annotation { "Feature Type Name" : "Feature", "Feature Type Description" : "" }
export const myFeature = defineFeature(function(context is Context, id is Id, definition is map)
    precondition{}
    {
        {
            var Q0;
            Q0=qCreatedBy(makeId("Top.planeOp"),FACE);
            var sketch = newSketch(context, id + "F0", { "sketchPlane" : qUnion([Q0])});
            skLineSegment(sketch, "E0", {"start": v(0, 56.35) * mm, "end": v(0, -56.35) * mm});
            skLineSegment(sketch, "E1", {"start": v(56.35, 0) * mm, "end": v(-56.35, 0) * mm});
            skPoint(sketch, "E2", {"position": v(0, 0) * mm});
            skPoint(sketch, "E3", {"position": v(-22.39, -33.62) * mm});
            skPoint(sketch, "E4", {"position": v(-22.39, 33.48) * mm});
            skPoint(sketch, "E5", {"position": v(21.85, 33.48) * mm});
            skLineSegment(sketch, "E6", {"start": v(1.95, 33.48) * mm, "end": v(7.67, 33.48) * mm});
            skLineSegment(sketch, "E7", {"start": v(21.85, -33.62) * mm, "end": v(1.95, -33.62) * mm});
            skLineSegment(sketch, "E8", {"start": v(21.85, 18.05) * mm, "end": v(21.85, 17.68) * mm});
            skLineSegment(sketch, "E9", {"start": v(-2.74, 33.48) * mm, "end": v(-21.16, 33.48) * mm});
            skLineSegment(sketch, "E10", {"start": v(-22.39, -33.62) * mm, "end": v(-10.07, -33.62) * mm});
            skLineSegment(sketch, "E11", {"start": v(-22.39, -2.3) * mm, "end": v(-22.39, -33.62) * mm});
            skPoint(sketch, "E12", {"position": v(-22.39, 31.95) * mm});
            skPoint(sketch, "E12.positionSnap0", {"position": v(-21.16, 31.95) * mm});
            skArc(sketch, "E13", {"start": v(-21.16, 33.48) * mm, "mid": v(-22.39, 31.95) * mm, "end": v(-21.16, 30.43) * mm});
            skPoint(sketch, "E14", {"position": v(-2.74, 33.48) * mm});
            skPoint(sketch, "E15", {"position": v(-7.3, 30.43) * mm});
            skLineSegment(sketch, "E16", {"start": v(-21.16, 30.43) * mm, "end": v(-7.3, 30.43) * mm});
            skPoint(sketch, "E17", {"position": v(-11.04, 20.68) * mm});
            skPoint(sketch, "E18", {"position": v(-9.45, 18.3) * mm});
            skPoint(sketch, "E19", {"position": v(-9.45, 25.39) * mm});
            skFitSpline(sketch, "E20", {"points": [v(-9.45, 25.39) * mm, v(-11.04, 20.68) * mm, v(-9.45, 18.3) * mm], "startDerivative": vector(-4.65, -9.06) * mm, "endDerivative": vector(5.1, -4.94) * mm});
            skLineSegment(sketch, "E21", {"start": v(-7.3, 30.43) * mm, "end": v(-9.45, 25.39) * mm});
            skPoint(sketch, "E22", {"position": v(-19.2, 12.85) * mm});
            skPoint(sketch, "E23", {"position": v(-12.14, 4.7) * mm});
            skArc(sketch, "E24", {"start": v(-19.2, 12.85) * mm, "mid": v(-8.74, 5.6) * mm, "end": v(-9.45, 18.3) * mm});
            skPoint(sketch, "E25", {"position": v(-8.14, 21.15) * mm});
            skPoint(sketch, "E26", {"position": v(-7.55, 20.43) * mm});
            skPoint(sketch, "E27", {"position": v(-7.55, 22.7) * mm});
            skFitSpline(sketch, "E28", {"points": [v(-7.55, 22.7) * mm, v(-8.14, 21.15) * mm, v(-7.55, 20.43) * mm], "startDerivative": vector(-1.74, -3) * mm, "endDerivative": vector(1.9, -1.47) * mm});
            skLineSegment(sketch, "E29", {"start": v(-2.74, 33.48) * mm, "end": v(-7.55, 22.7) * mm});
            skArc(sketch, "E30.0", {"start": v(-21.98, 12.85) * mm, "mid": v(-7.57, 3.08) * mm, "end": v(-7.62, 20.5) * mm});
            skPoint(sketch, "E31", {"position": v(-21.98, 12.85) * mm});
            skPoint(sketch, "E32", {"position": v(-20.63, 13.93) * mm});
            skArc(sketch, "E33", {"start": v(-19.2, 12.85) * mm, "mid": v(-20.59, 13.94) * mm, "end": v(-21.98, 12.85) * mm});
            skLineSegment(sketch, "E34", {"start": v(1.95, 33.48) * mm, "end": v(1.95, 2.25) * mm});
            skPoint(sketch, "E35", {"position": v(21.85, 18.05) * mm});
            skArc(sketch, "E36", {"start": v(13.56, 3.8) * mm, "mid": v(21.85, 17.87) * mm, "end": v(13.56, 31.93) * mm});
            skPoint(sketch, "E37", {"position": v(7.67, 33.48) * mm});
            skPoint(sketch, "E38", {"position": v(13.56, 31.93) * mm});
            skPoint(sketch, "E39", {"position": v(13.56, 3.8) * mm});
            skArc(sketch, "E40.0", {"start": v(5.03, 4.88) * mm, "mid": v(9.62, 5.44) * mm, "end": v(13.73, 7.58) * mm});
            skLineSegment(sketch, "E40.1", {"start": v(5.03, 27.26) * mm, "end": v(5.03, 4.88) * mm});
            skLineSegment(sketch, "E41", {"start": v(5.03, 27.26) * mm, "end": v(13.73, 7.58) * mm});
            skLineSegment(sketch, "E42", {"start": v(16.04, 9.89) * mm, "end": v(6.78, 30.83) * mm});
            skLineSegment(sketch, "E43", {"start": v(-22.39, -2.3) * mm, "end": v(-10.07, -2.3) * mm});
            skLineSegment(sketch, "E44", {"start": v(1.95, -2.3) * mm, "end": v(1.95, -33.62) * mm});
            skLineSegment(sketch, "E45", {"start": v(1.95, -2.3) * mm, "end": v(22.67, -2.3) * mm});
            skLineSegment(sketch, "E46", {"start": v(22.67, -2.3) * mm, "end": v(15.49, -17.1) * mm});
            skFitSpline(sketch, "E47", {"points": [v(15.49, -17.1) * mm, v(15.2, -17.6) * mm, v(15.17, -17.96) * mm], "startDerivative": vector(-0.63, -0.9) * mm, "endDerivative": vector(0.03, -0.82) * mm});
            skLineSegment(sketch, "E48.MirrorCS", {"start": v(1.95, -33.62) * mm, "end": v(22.67, -33.62) * mm});
            skLineSegment(sketch, "E49.MirrorCS", {"start": v(22.67, -33.62) * mm, "end": v(15.49, -18.82) * mm});
            skFitSpline(sketch, "E50.MirrorCS", {"points": [v(15.49, -18.82) * mm, v(15.2, -18.34) * mm, v(15.17, -17.96) * mm], "startDerivative": vector(-0.63, 0.9) * mm, "endDerivative": vector(0.03, 0.82) * mm});
            skArc(sketch, "E51", {"start": v(-5.17, -17.31) * mm, "mid": v(-2.75, -8.22) * mm, "end": v(-10.07, -2.3) * mm});
            skFitSpline(sketch, "E52", {"points": [v(-5.17, -17.31) * mm, v(-5.38, -17.68) * mm, v(-5.4, -17.96) * mm], "startDerivative": vector(-0.48, -0.68) * mm, "endDerivative": vector(0.02, -0.62) * mm});
            skArc(sketch, "E53.MirrorCS", {"start": v(-5.17, -18.61) * mm, "mid": v(-2.75, -27.7) * mm, "end": v(-10.07, -33.62) * mm});
            skFitSpline(sketch, "E54.MirrorCS", {"points": [v(-5.17, -18.61) * mm, v(-5.38, -18.25) * mm, v(-5.4, -17.96) * mm], "startDerivative": vector(-0.48, 0.68) * mm, "endDerivative": vector(0.02, 0.62) * mm});
            skPoint(sketch, "E55.end.orphan", {"position": v(-10.07, -33.62) * mm});
            skPoint(sketch, "E56.orphan", {"position": v(-10.07, -17.96) * mm});
            skPoint(sketch, "E57.orphan", {"position": v(0, -33.62) * mm});
            skLineSegment(sketch, "E58.MirrorCS", {"start": v(0, 2.62) * mm, "end": v(7.67, 2.62) * mm});
            skArc(sketch, "E59.trimOffspring", {"start": v(16.04, 9.89) * mm, "mid": v(17.67, 23.12) * mm, "end": v(6.78, 30.83) * mm});
            skPoint(sketch, "E60", {"position": v(7.67, 2.62) * mm});
            skFitSpline(sketch, "E61", {"points": [v(13.56, 3.8) * mm, v(10.55, 2.81) * mm, v(7.67, 2.62) * mm], "startDerivative": vector(-5.9, -2.33) * mm, "endDerivative": vector(-5.9, -0.02) * mm});
            skPoint(sketch, "E62.1.internal.snap0", {"position": v(9.38, 17.42) * mm});
            skFitSpline(sketch, "E62", {"points": [v(13.56, 31.93) * mm, v(9.38, 33.27) * mm, v(7.67, 33.48) * mm], "startDerivative": vector(-7.54, 2.7) * mm, "endDerivative": vector(-3.99, 0.22) * mm});
            skPoint(sketch, "E63.orphan", {"position": v(10.87, 2.62) * mm});
            skPoint(sketch, "E64.orphan", {"position": v(0, 33.48) * mm});
            skPoint(sketch, "E65.trimOffspring.start.orphan", {"position": v(21.85, 2.62) * mm});
            skLineSegment(sketch, "E66", {"start": v(-27.8, 0) * mm, "end": v(-27.8, 46.45) * mm});
            skLineSegment(sketch, "E67", {"start": v(-27.8, 46.45) * mm, "end": v(0, 46.45) * mm});
            skLineSegment(sketch, "E68.MirrorCS", {"start": v(27.8, 0) * mm, "end": v(27.8, 46.45) * mm});
            skLineSegment(sketch, "E69.MirrorCS", {"start": v(-27.8, -46.45) * mm, "end": v(0, -46.45) * mm});
            skLineSegment(sketch, "E70.MirrorCS", {"start": v(-27.8, 0) * mm, "end": v(-27.8, -46.45) * mm});
            skLineSegment(sketch, "E71.MirrorCS", {"start": v(27.8, 46.45) * mm, "end": v(0, 46.45) * mm});
            skLineSegment(sketch, "E72.MirrorCS", {"start": v(27.8, 0) * mm, "end": v(27.8, -46.45) * mm});
            skLineSegment(sketch, "E73.MirrorCS", {"start": v(27.8, -46.45) * mm, "end": v(0, -46.45) * mm});
            skSolve(sketch);
        }
        {
            var Q0;
            Q0=qCreatedBy(makeId("Top.planeOp"),FACE);
            var sketch = newSketch(context, id + "F1", { "sketchPlane" : qUnion([Q0])});
            skLineSegment(sketch, "E74.bottom", {"start": v(-27.8, 46.45) * mm, "end": v(27.8, 46.45) * mm});
            skLineSegment(sketch, "E74.top", {"start": v(-27.8, -46.45) * mm, "end": v(27.8, -46.45) * mm});
            skLineSegment(sketch, "E74.left", {"start": v(-27.8, 46.45) * mm, "end": v(-27.8, -46.45) * mm});
            skLineSegment(sketch, "E74.right", {"start": v(27.8, 46.45) * mm, "end": v(27.8, -46.45) * mm});
            skSolve(sketch);
        }
        {
            var Q0;
            Q0=makeQuery(id+"F1.imprint","IMPRINT",FACE,{"disambiguationData":[TD([[makeQuery(id+"F1.imprint","IMPRINT",EDGE,{"derivedFrom":sQuery(id+"F1.wireOp",EDGE,"E74.bottom")}),-1.0]])]});
            extrude(context, id + "F2", {"entities" : qUnion([Q0]), "oppositeDirection" : true, "depth" : 19.05 * mm, "offsetDistance" : 25.4 * mm});
        }
        {
            var Q0;
            {var subQ7=sQuery(id+"F0.wireOp",EDGE,"E6");Q0=makeQuery(id+"F0.imprint","IMPRINT",FACE,{"disambiguationData":[TD([[makeQuery(id+"F0.imprint","IMPRINT",EDGE,{"derivedFrom":subQ7}),-1.0]])]});}
            var Q1;
            Q1=makeQuery(id+"F0.imprint","IMPRINT",FACE,{"disambiguationData":[TD([[makeQuery(id+"F0.imprint","IMPRINT",EDGE,{"derivedFrom":sQuery(id+"F0.wireOp",EDGE,"E9")}),1.0]])]});
            var Q2;
            {var subQ0=sQuery(id+"F0.wireOp",EDGE,"E44");Q2=makeQuery(id+"F0.imprint","IMPRINT",FACE,{"disambiguationData":[TD([[makeQuery(id+"F0.imprint","IMPRINT",EDGE,{"derivedFrom":subQ0}),1.0]])]});}
            var Q3;
            Q3=makeQuery(id+"F0.imprint","IMPRINT",FACE,{"disambiguationData":[TD([[makeQuery(id+"F0.imprint","IMPRINT",EDGE,{"derivedFrom":sQuery(id+"F0.wireOp",EDGE,"E10")}),1.0]])]});
            extrude(context, id + "F3", {"entities" : qUnion([Q0, Q1, Q2, Q3]), "operationType" : NewBodyOperationType.ADD, "depth" : 5.08 * mm, "offsetDistance" : 25.4 * mm});
        }
        {
            var Q0;
            {var subQ3=sQuery(id+"F1.wireOp",EDGE,"E74.bottom");var subQ5=sQuery(id+"F1.wireOp",EDGE,"E74.left");var subQ6=sQuery(id+"F1.wireOp",EDGE,"E74.top");var subQ7=sQuery(id+"F1.wireOp",EDGE,"E74.right");Q0=makeQuery(id+"F3.boolean.opBoolean","SPLIT",FACE,{"disambiguationData":[TD([makeQuery(id+"F2.opExtrude","SWEPT_FACE",FACE,{"disambiguationData":[OSD([subQ3])]})])],"derivedFrom":makeQuery(id+"F2.opExtrude","CAP_FACE",FACE,{"disambiguationData":[OSD([subQ3,subQ6,subQ5,subQ7])],"isStart":true})});}
            var sketch = newSketch(context, id + "F4", { "sketchPlane" : qUnion([Q0])});
            skLineSegment(sketch, "E75", {"start": v(-27.8, 36.27) * mm, "end": v(27.8, 36.27) * mm});
            skLineSegment(sketch, "E76", {"start": v(-27.8, 36.27) * mm, "end": v(-27.8, 50.24) * mm});
            skLineSegment(sketch, "E77", {"start": v(-27.8, 50.24) * mm, "end": v(27.8, 50.24) * mm});
            skLineSegment(sketch, "E78", {"start": v(27.8, 50.24) * mm, "end": v(27.8, 36.27) * mm});
            skLineSegment(sketch, "E79.0", {"start": v(-24.8, 47.24) * mm, "end": v(24.8, 47.24) * mm});
            skLineSegment(sketch, "E79.1", {"start": v(-24.8, 39.27) * mm, "end": v(-24.8, 47.24) * mm});
            skLineSegment(sketch, "E79.2", {"start": v(-24.8, 39.27) * mm, "end": v(24.8, 39.27) * mm});
            skLineSegment(sketch, "E79.3", {"start": v(24.8, 47.24) * mm, "end": v(24.8, 39.27) * mm});
            skLineSegment(sketch, "E80", {"start": v(0, 0) * mm, "end": v(41.07, 0) * mm});
            skLineSegment(sketch, "E81.MirrorCS", {"start": v(-27.8, -50.24) * mm, "end": v(27.8, -50.24) * mm});
            skLineSegment(sketch, "E82.MirrorCS", {"start": v(-27.8, -36.27) * mm, "end": v(-27.8, -50.24) * mm});
            skLineSegment(sketch, "E83.MirrorCS", {"start": v(27.8, -50.24) * mm, "end": v(27.8, -36.27) * mm});
            skLineSegment(sketch, "E84.MirrorCS", {"start": v(-24.8, -39.27) * mm, "end": v(24.8, -39.27) * mm});
            skLineSegment(sketch, "E85.MirrorCS", {"start": v(-24.8, -39.27) * mm, "end": v(-24.8, -47.24) * mm});
            skLineSegment(sketch, "E86.MirrorCS", {"start": v(-24.8, -47.24) * mm, "end": v(24.8, -47.24) * mm});
            skLineSegment(sketch, "E87.MirrorCS", {"start": v(24.8, -47.24) * mm, "end": v(24.8, -39.27) * mm});
            skText(sketch, "E88", { "text": "Production", "fontName": "OpenSans-Regular.ttf"});
            skPoint(sketch, "E89", {"position": v(0, -39.27) * mm});
            skPoint(sketch, "E90", {"position": v(24.8, -43.26) * mm});
            skLineSegment(sketch, "E91", {"start": v(27.8, -36.27) * mm, "end": v(-27.8, -36.27) * mm});
            skText(sketch, "E92", { "text": "Bobby Saporito", "fontName": "OpenSans-Regular.ttf"});
            const initialGuessF4  = {"E88": [-0.01795, -0.04552, 1, 0, 0.00504], "E92": [-0.02514, 0.04098, 1, 0, 0.005]};
            skSetInitialGuess(sketch, initialGuessF4);
            skSolve(sketch);
        }
        {
            var Q0;
            Q0=makeQuery(id+"F4.imprint","IMPRINT",FACE,{"disambiguationData":[TD([[makeQuery(id+"F4.imprint","IMPRINT",EDGE,{"derivedFrom":sQuery(id+"F4.wireOp",EDGE,"e63348ab-3f83-47d4-992c-c16597fd5790.sketch_text.stroke-18")}),-1.0]])]});
            var Q1;
            Q1=makeQuery(id+"F4.imprint","IMPRINT",FACE,{"disambiguationData":[TD([[makeQuery(id+"F4.imprint","IMPRINT",EDGE,{"derivedFrom":sQuery(id+"F4.wireOp",EDGE,"e63348ab-3f83-47d4-992c-c16597fd5790.sketch_text.stroke-0")}),-1.0]])]});
            var Q2;
            Q2=makeQuery(id+"F4.imprint","IMPRINT",FACE,{"disambiguationData":[TD([[makeQuery(id+"F4.imprint","IMPRINT",EDGE,{"derivedFrom":sQuery(id+"F4.wireOp",EDGE,"e63348ab-3f83-47d4-992c-c16597fd5790.sketch_text.stroke-45")}),-1.0]])]});
            var Q3;
            Q3=makeQuery(id+"F4.imprint","IMPRINT",FACE,{"disambiguationData":[TD([[makeQuery(id+"F4.imprint","IMPRINT",EDGE,{"derivedFrom":sQuery(id+"F4.wireOp",EDGE,"e63348ab-3f83-47d4-992c-c16597fd5790.sketch_text.stroke-57")}),-1.0]])]});
            var Q4;
            Q4=makeQuery(id+"F4.imprint","IMPRINT",FACE,{"disambiguationData":[TD([[makeQuery(id+"F4.imprint","IMPRINT",EDGE,{"derivedFrom":sQuery(id+"F4.wireOp",EDGE,"e63348ab-3f83-47d4-992c-c16597fd5790.sketch_text.stroke-82")}),-1.0]])]});
            var Q5;
            Q5=makeQuery(id+"F4.imprint","IMPRINT",FACE,{"disambiguationData":[TD([[makeQuery(id+"F4.imprint","IMPRINT",EDGE,{"derivedFrom":sQuery(id+"F4.wireOp",EDGE,"e63348ab-3f83-47d4-992c-c16597fd5790.sketch_text.stroke-101")}),-1.0]])]});
            var Q6;
            Q6=makeQuery(id+"F4.imprint","IMPRINT",FACE,{"disambiguationData":[TD([[makeQuery(id+"F4.imprint","IMPRINT",EDGE,{"derivedFrom":sQuery(id+"F4.wireOp",EDGE,"e63348ab-3f83-47d4-992c-c16597fd5790.sketch_text.stroke-120")}),-1.0]])]});
            var Q7;
            Q7=makeQuery(id+"F4.imprint","IMPRINT",FACE,{"disambiguationData":[TD([[makeQuery(id+"F4.imprint","IMPRINT",EDGE,{"derivedFrom":sQuery(id+"F4.wireOp",EDGE,"e63348ab-3f83-47d4-992c-c16597fd5790.sketch_text.stroke-124")}),-1.0]])]});
            var Q8;
            Q8=makeQuery(id+"F4.imprint","IMPRINT",FACE,{"disambiguationData":[TD([[makeQuery(id+"F4.imprint","IMPRINT",EDGE,{"derivedFrom":sQuery(id+"F4.wireOp",EDGE,"e63348ab-3f83-47d4-992c-c16597fd5790.sketch_text.stroke-132")}),-1.0]])]});
            var Q9;
            Q9=makeQuery(id+"F4.imprint","IMPRINT",FACE,{"disambiguationData":[TD([[makeQuery(id+"F4.imprint","IMPRINT",EDGE,{"derivedFrom":sQuery(id+"F4.wireOp",EDGE,"e63348ab-3f83-47d4-992c-c16597fd5790.sketch_text.stroke-149")}),-1.0]])]});
            var Q10;
            Q10=makeQuery(id+"F4.imprint","IMPRINT",FACE,{"disambiguationData":[TD([[makeQuery(id+"F4.imprint","IMPRINT",EDGE,{"derivedFrom":sQuery(id+"F4.wireOp",EDGE,"e63348ab-3f83-47d4-992c-c16597fd5790.sketch_text.stroke-168")}),-1.0]])]});
            var Q11;
            {var subQ0=sQuery(id+"F4.wireOp",EDGE,"E76");Q11=makeQuery(id+"F4.imprint","IMPRINT",FACE,{"disambiguationData":[TD([[makeQuery(id+"F4.imprint","IMPRINT",EDGE,{"derivedFrom":subQ0}),1.0]])]});}
            var Q12;
            {var subQ2=sQuery(id+"F4.wireOp",EDGE,"E77");Q12=makeQuery(id+"F4.imprint","IMPRINT",FACE,{"disambiguationData":[TD([[makeQuery(id+"F4.imprint","IMPRINT",EDGE,{"derivedFrom":subQ2}),-1.0]])]});}
            extrude(context, id + "F5", {"entities" : qUnion([Q0, Q1, Q2, Q3, Q4, Q5, Q6, Q7, Q8, Q9, Q10, Q11, Q12]), "operationType" : NewBodyOperationType.ADD, "depth" : 3 * mm, "offsetDistance" : 25.4 * mm});
        }
        {
            var Q0;
            {var subQ1=sQuery(id+"F4.wireOp",EDGE,"E84.MirrorCS");Q0=makeQuery(id+"F4.imprint","IMPRINT",FACE,{"disambiguationData":[TD([[makeQuery(id+"F4.imprint","IMPRINT",EDGE,{"derivedFrom":subQ1}),1.0]])]});}
            var Q1;
            {var subQ8=sQuery(id+"F4.wireOp",EDGE,"E81.MirrorCS");Q1=makeQuery(id+"F4.imprint","IMPRINT",FACE,{"disambiguationData":[TD([[makeQuery(id+"F4.imprint","IMPRINT",EDGE,{"derivedFrom":subQ8}),1.0]])]});}
            var Q2;
            Q2=makeQuery(id+"F4.imprint","IMPRINT",FACE,{"disambiguationData":[TD([[makeQuery(id+"F4.imprint","IMPRINT",EDGE,{"derivedFrom":sQuery(id+"F4.wireOp",EDGE,"E88.sketch_text.stroke-0")}),-1.0]])]});
            var Q3;
            Q3=makeQuery(id+"F4.imprint","IMPRINT",FACE,{"disambiguationData":[TD([[makeQuery(id+"F4.imprint","IMPRINT",EDGE,{"derivedFrom":sQuery(id+"F4.wireOp",EDGE,"E88.sketch_text.stroke-14")}),-1.0]])]});
            var Q4;
            Q4=makeQuery(id+"F4.imprint","IMPRINT",FACE,{"disambiguationData":[TD([[makeQuery(id+"F4.imprint","IMPRINT",EDGE,{"derivedFrom":sQuery(id+"F4.wireOp",EDGE,"E88.sketch_text.stroke-33")}),-1.0]])]});
            var Q5;
            Q5=makeQuery(id+"F4.imprint","IMPRINT",FACE,{"disambiguationData":[TD([[makeQuery(id+"F4.imprint","IMPRINT",EDGE,{"derivedFrom":sQuery(id+"F4.wireOp",EDGE,"E88.sketch_text.stroke-58")}),-1.0]])]});
            var Q6;
            Q6=makeQuery(id+"F4.imprint","IMPRINT",FACE,{"disambiguationData":[TD([[makeQuery(id+"F4.imprint","IMPRINT",EDGE,{"derivedFrom":sQuery(id+"F4.wireOp",EDGE,"E88.sketch_text.stroke-62")}),-1.0]])]});
            var Q7;
            Q7=makeQuery(id+"F4.imprint","IMPRINT",FACE,{"disambiguationData":[TD([[makeQuery(id+"F4.imprint","IMPRINT",EDGE,{"derivedFrom":sQuery(id+"F4.wireOp",EDGE,"E88.sketch_text.stroke-114")}),-1.0]])]});
            var Q8;
            Q8=makeQuery(id+"F4.imprint","IMPRINT",FACE,{"disambiguationData":[TD([[makeQuery(id+"F4.imprint","IMPRINT",EDGE,{"derivedFrom":sQuery(id+"F4.wireOp",EDGE,"E88.sketch_text.stroke-70")}),-1.0]])]});
            var Q9;
            {var subQ6=sQuery(id+"F4.wireOp",EDGE,"E88.sketch_text.stroke-84");Q9=makeQuery(id+"F4.imprint","IMPRINT",FACE,{"disambiguationData":[TD([[makeQuery(id+"F4.imprint","IMPRINT",EDGE,{"derivedFrom":subQ6}),-1.0]])]});}
            extrude(context, id + "F6", {"entities" : qUnion([Q0, Q1, Q2, Q3, Q4, Q5, Q6, Q7, Q8, Q9]), "operationType" : NewBodyOperationType.ADD, "depth" : 3 * mm, "offsetDistance" : 25.4 * mm});
        }
        {
            var Q0;
            Q0=makeQuery(id+"F5.opExtrude","CAP_FACE",FACE,{"disambiguationData":[OSD([sQuery(id+"F4.wireOp",EDGE,"E75"),sQuery(id+"F4.wireOp",EDGE,"E76"),sQuery(id+"F4.wireOp",EDGE,"E77"),sQuery(id+"F4.wireOp",EDGE,"E78"),sQuery(id+"F4.wireOp",EDGE,"E79.0"),sQuery(id+"F4.wireOp",EDGE,"E79.1"),sQuery(id+"F4.wireOp",EDGE,"E79.2"),sQuery(id+"F4.wireOp",EDGE,"E79.3")])],"isStart":true});
            var sketch = newSketch(context, id + "F7", { "sketchPlane" : qUnion([Q0])});
            skLineSegment(sketch, "E93.bottom", {"start": v(27.8, -50.24) * mm, "end": v(-27.8, -50.24) * mm});
            skLineSegment(sketch, "E93.top", {"start": v(27.8, -46.45) * mm, "end": v(-27.8, -46.45) * mm});
            skLineSegment(sketch, "E93.left", {"start": v(27.8, -50.24) * mm, "end": v(27.8, -46.45) * mm});
            skLineSegment(sketch, "E93.right", {"start": v(-27.8, -50.24) * mm, "end": v(-27.8, -46.45) * mm});
            skSolve(sketch);
        }
        {
            var Q0;
            Q0=qSketchRegion(id+"F7",true);
            var Q1;
            Q1=makeQuery(id+"F2.opExtrude","CAP_FACE",FACE,{"disambiguationData":[OSD([sQuery(id+"F1.wireOp",EDGE,"E74.bottom"),sQuery(id+"F1.wireOp",EDGE,"E74.top"),sQuery(id+"F1.wireOp",EDGE,"E74.left"),sQuery(id+"F1.wireOp",EDGE,"E74.right")])],"isStart":false});
            extrude(context, id + "F8", {"entities" : qUnion([Q0]), "operationType" : NewBodyOperationType.ADD, "endBound" : BoundingType.UP_TO_SURFACE, "depth" : 25.4 * mm, "endBoundEntityFace" : qUnion([Q1]), "offsetDistance" : 25.4 * mm});
        }
        {
            var Q0;
            Q0=makeQuery(id+"F6.opExtrude","CAP_FACE",FACE,{"disambiguationData":[OSD([sQuery(id+"F4.wireOp",EDGE,"E81.MirrorCS"),sQuery(id+"F4.wireOp",EDGE,"E82.MirrorCS"),sQuery(id+"F4.wireOp",EDGE,"E83.MirrorCS"),sQuery(id+"F4.wireOp",EDGE,"E84.MirrorCS"),sQuery(id+"F4.wireOp",EDGE,"E85.MirrorCS"),sQuery(id+"F4.wireOp",EDGE,"E86.MirrorCS"),sQuery(id+"F4.wireOp",EDGE,"E87.MirrorCS"),sQuery(id+"F4.wireOp",EDGE,"E91")])],"isStart":true});
            var sketch = newSketch(context, id + "F9", { "sketchPlane" : qUnion([Q0])});
            skLineSegment(sketch, "E94.bottom", {"start": v(-27.8, 50.24) * mm, "end": v(27.8, 50.24) * mm});
            skLineSegment(sketch, "E94.top", {"start": v(-27.8, 46.45) * mm, "end": v(27.8, 46.45) * mm});
            skLineSegment(sketch, "E94.left", {"start": v(-27.8, 50.24) * mm, "end": v(-27.8, 46.45) * mm});
            skLineSegment(sketch, "E94.right", {"start": v(27.8, 50.24) * mm, "end": v(27.8, 46.45) * mm});
            skSolve(sketch);
        }
        {
            var Q0;
            Q0=qSketchRegion(id+"F9",true);
            var Q1;
            Q1=makeQuery(id+"F8.boolean.opBoolean","MERGE",FACE,{"derivedFrom":[makeQuery(id+"F2.opExtrude","CAP_FACE",FACE,{"disambiguationData":[OSD([sQuery(id+"F1.wireOp",EDGE,"E74.bottom"),sQuery(id+"F1.wireOp",EDGE,"E74.top"),sQuery(id+"F1.wireOp",EDGE,"E74.left"),sQuery(id+"F1.wireOp",EDGE,"E74.right")])],"isStart":false}),makeQuery(id+"F8.opExtrude","CAP_FACE",FACE,{"disambiguationData":[OSD([sQuery(id+"F7.wireOp",EDGE,"E93.bottom"),sQuery(id+"F7.wireOp",EDGE,"E93.top"),sQuery(id+"F7.wireOp",EDGE,"E93.left"),sQuery(id+"F7.wireOp",EDGE,"E93.right")])],"isStart":false})]});
            extrude(context, id + "F10", {"entities" : qUnion([Q0]), "operationType" : NewBodyOperationType.ADD, "endBound" : BoundingType.UP_TO_SURFACE, "depth" : 25.4 * mm, "endBoundEntityFace" : qUnion([Q1]), "offsetDistance" : 25.4 * mm});
        }
        {
            var Q0;
            Q0=makeQuery(id+"F10.boolean.opBoolean","MERGE",FACE,{"derivedFrom":[makeQuery(id+"F6.opExtrude","SWEPT_FACE",FACE,{"disambiguationData":[OSD([sQuery(id+"F4.wireOp",EDGE,"E81.MirrorCS")])]}),makeQuery(id+"F10.opExtrude","SWEPT_FACE",FACE,{"disambiguationData":[OSD([sQuery(id+"F9.wireOp",EDGE,"E94.bottom")])]})]});
            var sketch = newSketch(context, id + "F11", { "sketchPlane" : qUnion([Q0])});
            skLineSegment(sketch, "E95", {"start": v(-27.8, 0) * mm, "end": v(27.8, 0) * mm});
            skPoint(sketch, "E96", {"position": v(27.8, 0) * mm});
            skPoint(sketch, "E97", {"position": v(27.8, -19.05) * mm});
            skLineSegment(sketch, "E98", {"start": v(27.8, -9.42) * mm, "end": v(11.93, -9.42) * mm});
            skLineSegment(sketch, "E99", {"start": v(11.93, -9.42) * mm, "end": v(11.93, -1.48) * mm});
            skLineSegment(sketch, "E100", {"start": v(11.93, -1.48) * mm, "end": v(27.8, -1.48) * mm});
            skLineSegment(sketch, "E101", {"start": v(27.8, -1.48) * mm, "end": v(27.8, -9.42) * mm});
            skLineSegment(sketch, "E102.MirrorCS", {"start": v(11.93, -17.36) * mm, "end": v(27.8, -17.36) * mm});
            skLineSegment(sketch, "E103.MirrorCS", {"start": v(11.93, -9.42) * mm, "end": v(11.93, -17.36) * mm});
            skSolve(sketch);
        }
        {
            var Q0;
            Q0=makeQuery(id+"F11.imprint","IMPRINT",FACE,{"disambiguationData":[TD([[makeQuery(id+"F11.imprint","IMPRINT",EDGE,{"derivedFrom":sQuery(id+"F11.wireOp",EDGE,"E98")}),-1.0]])]});
            var Q1;
            {var subQ0=sQuery(id+"F11.wireOp",EDGE,"E98");Q1=makeQuery(id+"F11.imprint","IMPRINT",FACE,{"disambiguationData":[TD([[makeQuery(id+"F11.imprint","IMPRINT",EDGE,{"derivedFrom":subQ0}),1.0]])]});}
            var Q2;
            Q2=makeQuery(id+"F5.opExtrude","SWEPT_FACE",FACE,{"disambiguationData":[OSD([sQuery(id+"F4.wireOp",EDGE,"E75")])]});
            extrude(context, id + "F12", {"entities" : qUnion([Q0, Q1]), "operationType" : NewBodyOperationType.REMOVE, "endBound" : BoundingType.UP_TO_SURFACE, "oppositeDirection" : true, "depth" : 25.4 * mm, "endBoundEntityFace" : qUnion([Q2]), "offsetDistance" : 25.4 * mm});
        }
        {
            var Q0;
            Q0=makeQuery(id+"F4.imprint","IMPRINT",FACE,{"disambiguationData":[TD([[makeQuery(id+"F4.imprint","IMPRINT",EDGE,{"derivedFrom":sQuery(id+"F4.wireOp",EDGE,"E92.sketch_text.stroke-0")}),-1.0]])]});
            var Q1;
            Q1=makeQuery(id+"F4.imprint","IMPRINT",FACE,{"disambiguationData":[TD([[makeQuery(id+"F4.imprint","IMPRINT",EDGE,{"derivedFrom":sQuery(id+"F4.wireOp",EDGE,"E92.sketch_text.stroke-25")}),-1.0]])]});
            var Q2;
            Q2=makeQuery(id+"F4.imprint","IMPRINT",FACE,{"disambiguationData":[TD([[makeQuery(id+"F4.imprint","IMPRINT",EDGE,{"derivedFrom":sQuery(id+"F4.wireOp",EDGE,"E92.sketch_text.stroke-42")}),-1.0]])]});
            var Q3;
            Q3=makeQuery(id+"F4.imprint","IMPRINT",FACE,{"disambiguationData":[TD([[makeQuery(id+"F4.imprint","IMPRINT",EDGE,{"derivedFrom":sQuery(id+"F4.wireOp",EDGE,"E92.sketch_text.stroke-65")}),-1.0]])]});
            var Q4;
            Q4=makeQuery(id+"F4.imprint","IMPRINT",FACE,{"disambiguationData":[TD([[makeQuery(id+"F4.imprint","IMPRINT",EDGE,{"derivedFrom":sQuery(id+"F4.wireOp",EDGE,"E92.sketch_text.stroke-181")}),-1.0]])]});
            var Q5;
            Q5=makeQuery(id+"F4.imprint","IMPRINT",FACE,{"disambiguationData":[TD([[makeQuery(id+"F4.imprint","IMPRINT",EDGE,{"derivedFrom":sQuery(id+"F4.wireOp",EDGE,"E92.sketch_text.stroke-198")}),-1.0]])]});
            var Q6;
            Q6=makeQuery(id+"F4.imprint","IMPRINT",FACE,{"disambiguationData":[TD([[makeQuery(id+"F4.imprint","IMPRINT",EDGE,{"derivedFrom":sQuery(id+"F4.wireOp",EDGE,"E92.sketch_text.stroke-211")}),-1.0]])]});
            var Q7;
            Q7=makeQuery(id+"F4.imprint","IMPRINT",FACE,{"disambiguationData":[TD([[makeQuery(id+"F4.imprint","IMPRINT",EDGE,{"derivedFrom":sQuery(id+"F4.wireOp",EDGE,"E92.sketch_text.stroke-223")}),-1.0]])]});
            var Q8;
            Q8=makeQuery(id+"F4.imprint","IMPRINT",FACE,{"disambiguationData":[TD([[makeQuery(id+"F4.imprint","IMPRINT",EDGE,{"derivedFrom":sQuery(id+"F4.wireOp",EDGE,"E92.sketch_text.stroke-215")}),-1.0]])]});
            var Q9;
            Q9=makeQuery(id+"F4.imprint","IMPRINT",FACE,{"disambiguationData":[TD([[makeQuery(id+"F4.imprint","IMPRINT",EDGE,{"derivedFrom":sQuery(id+"F4.wireOp",EDGE,"E92.sketch_text.stroke-242")}),-1.0]])]});
            var Q10;
            Q10=makeQuery(id+"F4.imprint","IMPRINT",FACE,{"disambiguationData":[TD([[makeQuery(id+"F4.imprint","IMPRINT",EDGE,{"derivedFrom":sQuery(id+"F4.wireOp",EDGE,"E92.sketch_text.stroke-88")}),-1.0]])]});
            var Q11;
            Q11=makeQuery(id+"F4.imprint","IMPRINT",FACE,{"disambiguationData":[TD([[makeQuery(id+"F4.imprint","IMPRINT",EDGE,{"derivedFrom":sQuery(id+"F4.wireOp",EDGE,"E92.sketch_text.stroke-104")}),-1.0]])]});
            var Q12;
            Q12=makeQuery(id+"F4.imprint","IMPRINT",FACE,{"disambiguationData":[TD([[makeQuery(id+"F4.imprint","IMPRINT",EDGE,{"derivedFrom":sQuery(id+"F4.wireOp",EDGE,"E92.sketch_text.stroke-129")}),-1.0]])]});
            var Q13;
            Q13=makeQuery(id+"F4.imprint","IMPRINT",FACE,{"disambiguationData":[TD([[makeQuery(id+"F4.imprint","IMPRINT",EDGE,{"derivedFrom":sQuery(id+"F4.wireOp",EDGE,"E92.sketch_text.stroke-156")}),-1.0]])]});
            extrude(context, id + "F13", {"entities" : qUnion([Q0, Q1, Q2, Q3, Q4, Q5, Q6, Q7, Q8, Q9, Q10, Q11, Q12, Q13]), "operationType" : NewBodyOperationType.ADD, "depth" : 3 * mm, "offsetDistance" : 25.4 * mm});
        }
        {
            var Q0;
            Q0=makeQuery(id+"F4.imprint","IMPRINT",FACE,{"disambiguationData":[TD([[makeQuery(id+"F4.imprint","IMPRINT",EDGE,{"derivedFrom":sQuery(id+"F4.wireOp",EDGE,"E88.sketch_text.stroke-0")}),-1.0]])]});
            var Q1;
            Q1=makeQuery(id+"F4.imprint","IMPRINT",FACE,{"disambiguationData":[TD([[makeQuery(id+"F4.imprint","IMPRINT",EDGE,{"derivedFrom":sQuery(id+"F4.wireOp",EDGE,"E88.sketch_text.stroke-15")}),-1.0]])]});
            var Q2;
            Q2=makeQuery(id+"F4.imprint","IMPRINT",FACE,{"disambiguationData":[TD([[makeQuery(id+"F4.imprint","IMPRINT",EDGE,{"derivedFrom":sQuery(id+"F4.wireOp",EDGE,"E88.sketch_text.stroke-28")}),-1.0]])]});
            var Q3;
            Q3=makeQuery(id+"F4.imprint","IMPRINT",FACE,{"disambiguationData":[TD([[makeQuery(id+"F4.imprint","IMPRINT",EDGE,{"derivedFrom":sQuery(id+"F4.wireOp",EDGE,"E88.sketch_text.stroke-45")}),-1.0]])]});
            var Q4;
            Q4=makeQuery(id+"F4.imprint","IMPRINT",FACE,{"disambiguationData":[TD([[makeQuery(id+"F4.imprint","IMPRINT",EDGE,{"derivedFrom":sQuery(id+"F4.wireOp",EDGE,"E88.sketch_text.stroke-69")}),-1.0]])]});
            var Q5;
            Q5=makeQuery(id+"F4.imprint","IMPRINT",FACE,{"disambiguationData":[TD([[makeQuery(id+"F4.imprint","IMPRINT",EDGE,{"derivedFrom":sQuery(id+"F4.wireOp",EDGE,"E88.sketch_text.stroke-86")}),-1.0]])]});
            var Q6;
            Q6=makeQuery(id+"F4.imprint","IMPRINT",FACE,{"disambiguationData":[TD([[makeQuery(id+"F4.imprint","IMPRINT",EDGE,{"derivedFrom":sQuery(id+"F4.wireOp",EDGE,"E88.sketch_text.stroke-101")}),-1.0]])]});
            var Q7;
            Q7=makeQuery(id+"F4.imprint","IMPRINT",FACE,{"disambiguationData":[TD([[makeQuery(id+"F4.imprint","IMPRINT",EDGE,{"derivedFrom":sQuery(id+"F4.wireOp",EDGE,"E88.sketch_text.stroke-120")}),-1.0]])]});
            var Q8;
            Q8=makeQuery(id+"F4.imprint","IMPRINT",FACE,{"disambiguationData":[TD([[makeQuery(id+"F4.imprint","IMPRINT",EDGE,{"derivedFrom":sQuery(id+"F4.wireOp",EDGE,"E88.sketch_text.stroke-124")}),-1.0]])]});
            var Q9;
            Q9=makeQuery(id+"F4.imprint","IMPRINT",FACE,{"disambiguationData":[TD([[makeQuery(id+"F4.imprint","IMPRINT",EDGE,{"derivedFrom":sQuery(id+"F4.wireOp",EDGE,"E88.sketch_text.stroke-132")}),-1.0]])]});
            var Q10;
            Q10=makeQuery(id+"F4.imprint","IMPRINT",FACE,{"disambiguationData":[TD([[makeQuery(id+"F4.imprint","IMPRINT",EDGE,{"derivedFrom":sQuery(id+"F4.wireOp",EDGE,"E88.sketch_text.stroke-149")}),-1.0]])]});
            extrude(context, id + "F14", {"entities" : qUnion([Q0, Q1, Q2, Q3, Q4, Q5, Q6, Q7, Q8, Q9, Q10]), "operationType" : NewBodyOperationType.ADD, "depth" : 3 * mm, "offsetDistance" : 25.4 * mm});
        }
    });